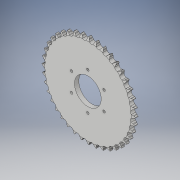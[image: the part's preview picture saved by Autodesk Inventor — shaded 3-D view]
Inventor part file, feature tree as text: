
AUTODESK INVENTOR PART (.ipt)
format: ipt  version: 2019 (Build 230136000, 136)  size: 900,608 bytes
history: native  units: in
note: dims shown in document units (in); Inventor stores cm internally (conversion verified against a paired STEP export)
features: other x2, extrude x2, sketch x2, pattern_circular x1
ambient origin geometry x8: Origin, YZ Plane, XZ Plane, XY Plane, X Axis, Y Axis, Z Axis, Center Point
bodies: Solid1 (feature_tree)
feature tree (7):
  other  "2299K810_MACHINABLE-BORE FLAT SPROCKET1"
  extrude  "Extrusion1"  Depth=1.0in TaperAngle=0.0deg
  extrude  "Extrusion2"  Depth=1.0in
  pattern_circular  "Circular Pattern1"  [2 undecoded]
  other  "Cut-Extrude2"
  sketch  "Sketch1"  dims[d0=2.85in d1=1.0in d2=0.0in]
  sketch  "Sketch2"  dims[d3=4.0in d4=0.266in d5=1.0in d6=0.0in d7=2.3622in d8=360.0deg]
note: 2 required parameter values undecoded (feature->parameter linkage not recoverable at this tier; creation-order binding heuristic only, values carry confidence <= 0.55)
